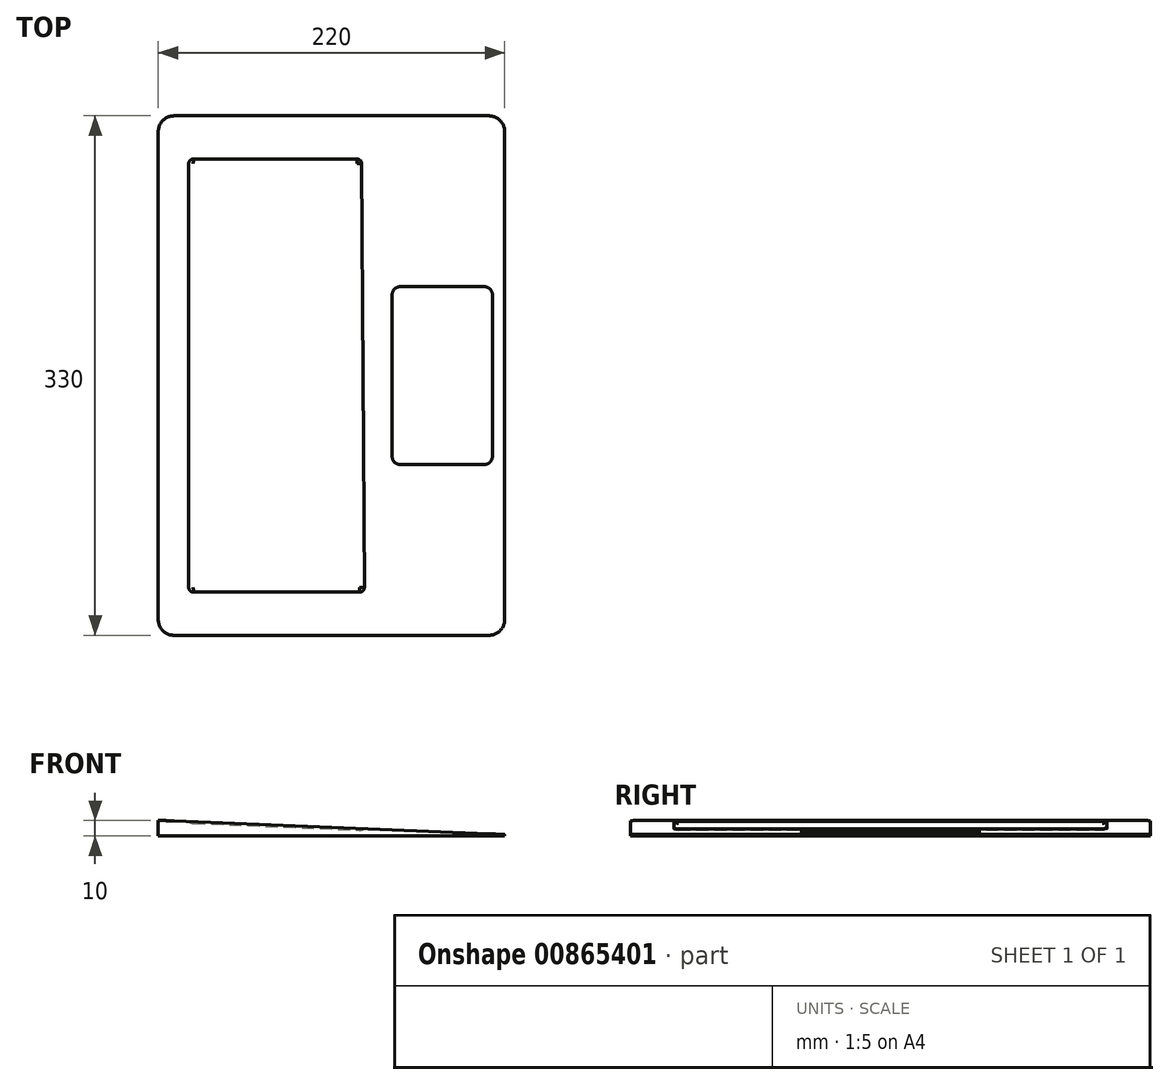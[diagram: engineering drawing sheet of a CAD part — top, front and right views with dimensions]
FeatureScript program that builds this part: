
annotation { "Feature Type Name" : "Feature", "Feature Type Description" : "" }
export const myFeature = defineFeature(function(context is Context, id is Id, definition is map)
    precondition{}
    {
        {
            var Q0;
            Q0=qCreatedBy(makeId("Front.planeOp"),FACE);
            var sketch = newSketch(context, id + "F0", { "sketchPlane" : qUnion([Q0])});
            skLineSegment(sketch, "E0", {"start": v(-46.92, 6.77) * mm, "end": v(-46.92, -3.23) * mm});
            skLineSegment(sketch, "E1", {"start": v(-46.92, -3.23) * mm, "end": v(173.08, -3.23) * mm});
            skLineSegment(sketch, "E2", {"start": v(173.08, -3.23) * mm, "end": v(173.08, -2.23) * mm});
            skLineSegment(sketch, "E3", {"start": v(173.08, -2.23) * mm, "end": v(-46.92, 6.77) * mm});
            skSolve(sketch);
        }
        {
            var Q0;
            Q0=makeQuery(id+"F0.imprint","IMPRINT",FACE,{"disambiguationData":[TD([[makeQuery(id+"F0.imprint","IMPRINT",EDGE,{"derivedFrom":sQuery(id+"F0.wireOp",EDGE,"E0")}),1.0]])]});
            extrude(context, id + "F1", {"entities" : qUnion([Q0]), "oppositeDirection" : true, "depth" : 330 * mm, "offsetDistance" : 25 * mm});
        }
        {
            var Q0;
            Q0=makeQuery(id+"F1.opExtrude","CAP_EDGE",EDGE,{"disambiguationData":[OSD([sQuery(id+"F0.wireOp",EDGE,"E0")])],"isStart":true});
            fillet(context, id + "F2", {"entities" : qUnion([Q0]), "radius" : 10 * mm, "tangentPropagation" : true, "allowEdgeOverflow" : false});
        }
        {
            var Q0;
            Q0=makeQuery(id+"F1.opExtrude","CAP_EDGE",EDGE,{"disambiguationData":[OSD([sQuery(id+"F0.wireOp",EDGE,"E0")])],"isStart":false});
            fillet(context, id + "F3", {"entities" : qUnion([Q0]), "radius" : 10 * mm, "tangentPropagation" : true, "allowEdgeOverflow" : false});
        }
        {
            var Q0;
            Q0=makeQuery(id+"F1.opExtrude","SWEPT_FACE",FACE,{"disambiguationData":[OSD([sQuery(id+"F0.wireOp",EDGE,"E3")])]});
            var sketch = newSketch(context, id + "F4", { "sketchPlane" : qUnion([Q0])});
            skLineSegment(sketch, "E4", {"start": v(0, 0) * mm, "end": v(-46.11, 10) * mm});
            skLineSegment(sketch, "E5", {"start": v(-46.11, 10) * mm, "end": v(-46.11, 0) * mm});
            skLineSegment(sketch, "E6", {"start": v(-46.11, 0) * mm, "end": v(-46.11, 330) * mm});
            skLineSegment(sketch, "E7", {"start": v(-46.11, 330) * mm, "end": v(173.89, 330) * mm});
            skLineSegment(sketch, "E8", {"start": v(173.89, 330) * mm, "end": v(173.89, 0) * mm});
            skLineSegment(sketch, "E9", {"start": v(173.89, 0) * mm, "end": v(-46.11, 0) * mm});
            skLineSegment(sketch, "E10", {"start": v(173.89, 330) * mm, "end": v(-46.11, 0) * mm});
            skLineSegment(sketch, "E11", {"start": v(-46.11, 0) * mm, "end": v(-27.8, 27.46) * mm});
            skLineSegment(sketch, "E12", {"start": v(173.89, 330) * mm, "end": v(155.58, 302.54) * mm});
            skLineSegment(sketch, "E13", {"start": v(-46.11, 330) * mm, "end": v(173.89, 0) * mm});
            skLineSegment(sketch, "E14", {"start": v(-46.11, 330) * mm, "end": v(-27.8, 302.54) * mm});
            skLineSegment(sketch, "E15", {"start": v(173.89, 0) * mm, "end": v(155.58, 27.46) * mm});
            skLineSegment(sketch, "E16", {"start": v(-27.8, 302.54) * mm, "end": v(-27.8, 27.46) * mm});
            skLineSegment(sketch, "E17", {"start": v(-27.8, 27.46) * mm, "end": v(83.9, 27.46) * mm});
            skLineSegment(sketch, "E18", {"start": v(-27.8, 302.54) * mm, "end": v(82.2, 302.54) * mm});
            skLineSegment(sketch, "E19", {"start": v(82.2, 302.54) * mm, "end": v(83.9, 27.46) * mm});
            skLineSegment(sketch, "E20", {"start": v(83.23, 135.99) * mm, "end": v(101.53, 108.53) * mm});
            skLineSegment(sketch, "E21", {"start": v(101.53, 108.53) * mm, "end": v(101.53, 221.47) * mm});
            skLineSegment(sketch, "E22", {"start": v(101.53, 221.47) * mm, "end": v(165.25, 221.47) * mm});
            skLineSegment(sketch, "E23", {"start": v(165.25, 221.47) * mm, "end": v(165.25, 108.53) * mm});
            skLineSegment(sketch, "E24", {"start": v(165.25, 108.53) * mm, "end": v(101.53, 108.53) * mm});
            skSolve(sketch);
        }
        {
            var Q0;
            {var subQ5=sQuery(id+"F4.wireOp",EDGE,"E18");Q0=makeQuery(id+"F4.imprint","IMPRINT",FACE,{"disambiguationData":[TD([[makeQuery(id+"F4.imprint","IMPRINT",EDGE,{"derivedFrom":subQ5}),-1.0]])]});}
            var Q1;
            {var subQ0=sQuery(id+"F4.wireOp",EDGE,"E16");Q1=makeQuery(id+"F4.imprint","IMPRINT",FACE,{"disambiguationData":[TD([[makeQuery(id+"F4.imprint","IMPRINT",EDGE,{"derivedFrom":subQ0}),1.0]])]});}
            var Q2;
            {var subQ0=sQuery(id+"F4.wireOp",EDGE,"E19");var subQ1=sQuery(id+"F4.wireOp",EDGE,"E10");var subQ2=makeQuery(id+"F4.imprint","INTERSECT",VERTEX,{"derivedFrom":[subQ1,subQ0]});Q2=makeQuery(id+"F4.imprint","IMPRINT",FACE,{"disambiguationData":[TD([[makeQuery(id+"F4.imprint","IMPRINT",EDGE,{"disambiguationData":[TD([[subQ2,-1.0]])],"derivedFrom":subQ1}),1.0]])]});}
            var Q3;
            {var subQ0=sQuery(id+"F4.wireOp",EDGE,"E17");Q3=makeQuery(id+"F4.imprint","IMPRINT",FACE,{"disambiguationData":[TD([[makeQuery(id+"F4.imprint","IMPRINT",EDGE,{"derivedFrom":subQ0}),1.0]])]});}
            extrude(context, id + "F5", {"entities" : qUnion([Q0, Q1, Q2, Q3]), "operationType" : NewBodyOperationType.REMOVE, "oppositeDirection" : true, "depth" : 1 * mm, "offsetDistance" : 25 * mm});
        }
        {
            var Q0;
            Q0=makeQuery(id+"F5.boolean.opBoolean","COPY",EDGE,{"derivedFrom":makeQuery(id+"F5.opExtrude","CAP_EDGE",EDGE,{"disambiguationData":[OSD([sQuery(id+"F4.wireOp",EDGE,"E16")])],"isStart":false})});
            var Q1;
            Q1=makeQuery(id+"F5.boolean.opBoolean","COPY",EDGE,{"derivedFrom":makeQuery(id+"F5.opExtrude","CAP_EDGE",EDGE,{"disambiguationData":[OSD([sQuery(id+"F4.wireOp",EDGE,"E17")])],"isStart":false})});
            var Q2;
            Q2=makeQuery(id+"F5.boolean.opBoolean","COPY",EDGE,{"derivedFrom":makeQuery(id+"F5.opExtrude","CAP_EDGE",EDGE,{"disambiguationData":[OSD([sQuery(id+"F4.wireOp",EDGE,"E19")])],"isStart":false})});
            var Q3;
            Q3=makeQuery(id+"F5.boolean.opBoolean","COPY",EDGE,{"derivedFrom":makeQuery(id+"F5.opExtrude","CAP_EDGE",EDGE,{"disambiguationData":[OSD([sQuery(id+"F4.wireOp",EDGE,"E18")])],"isStart":false})});
            fillet(context, id + "F6", {"entities" : qUnion([Q0, Q1, Q2, Q3]), "radius" : 5 * mm, "tangentPropagation" : true, "allowEdgeOverflow" : false});
        }
        {
            var Q0;
            Q0=makeQuery(id+"F4.imprint","IMPRINT",FACE,{"disambiguationData":[TD([[makeQuery(id+"F4.imprint","IMPRINT",EDGE,{"derivedFrom":sQuery(id+"F4.wireOp",EDGE,"E21")}),-1.0]])]});
            extrude(context, id + "F7", {"entities" : qUnion([Q0]), "operationType" : NewBodyOperationType.REMOVE, "oppositeDirection" : true, "depth" : 0.5 * mm, "offsetDistance" : 25 * mm});
        }
        {
            var Q0;
            Q0=makeQuery(id+"F6.opFillet","BLEND_EDGE",EDGE,{"blendedFrom":[makeQuery(id+"F5.boolean.opBoolean","COPY",EDGE,{"derivedFrom":makeQuery(id+"F5.opExtrude","CAP_EDGE",EDGE,{"disambiguationData":[OSD([sQuery(id+"F4.wireOp",EDGE,"E17")])],"isStart":false})}),makeQuery(id+"F5.boolean.opBoolean","COPY",EDGE,{"derivedFrom":makeQuery(id+"F5.opExtrude","CAP_EDGE",EDGE,{"disambiguationData":[OSD([sQuery(id+"F4.wireOp",EDGE,"E19")])],"isStart":false})})],"blendedInto":[]});
            fillet(context, id + "F8", {"entities" : qUnion([Q0]), "radius" : 5 * mm, "tangentPropagation" : true, "allowEdgeOverflow" : false});
        }
        {
            var Q0;
            Q0=makeQuery(id+"F6.opFillet","BLEND_EDGE",EDGE,{"blendedFrom":[makeQuery(id+"F5.boolean.opBoolean","COPY",EDGE,{"derivedFrom":makeQuery(id+"F5.opExtrude","CAP_EDGE",EDGE,{"disambiguationData":[OSD([sQuery(id+"F4.wireOp",EDGE,"E18")])],"isStart":false})}),makeQuery(id+"F5.boolean.opBoolean","COPY",EDGE,{"derivedFrom":makeQuery(id+"F5.opExtrude","CAP_EDGE",EDGE,{"disambiguationData":[OSD([sQuery(id+"F4.wireOp",EDGE,"E19")])],"isStart":false})})],"blendedInto":[]});
            var Q1;
            Q1=makeQuery(id+"F6.opFillet","BLEND_EDGE",EDGE,{"blendedFrom":[makeQuery(id+"F5.boolean.opBoolean","COPY",EDGE,{"derivedFrom":makeQuery(id+"F5.opExtrude","CAP_EDGE",EDGE,{"disambiguationData":[OSD([sQuery(id+"F4.wireOp",EDGE,"E16")])],"isStart":false})}),makeQuery(id+"F5.boolean.opBoolean","COPY",EDGE,{"derivedFrom":makeQuery(id+"F5.opExtrude","CAP_EDGE",EDGE,{"disambiguationData":[OSD([sQuery(id+"F4.wireOp",EDGE,"E18")])],"isStart":false})})],"blendedInto":[]});
            var Q2;
            Q2=makeQuery(id+"F6.opFillet","BLEND_EDGE",EDGE,{"blendedFrom":[makeQuery(id+"F5.boolean.opBoolean","COPY",EDGE,{"derivedFrom":makeQuery(id+"F5.opExtrude","CAP_EDGE",EDGE,{"disambiguationData":[OSD([sQuery(id+"F4.wireOp",EDGE,"E16")])],"isStart":false})}),makeQuery(id+"F5.boolean.opBoolean","COPY",EDGE,{"derivedFrom":makeQuery(id+"F5.opExtrude","CAP_EDGE",EDGE,{"disambiguationData":[OSD([sQuery(id+"F4.wireOp",EDGE,"E17")])],"isStart":false})})],"blendedInto":[]});
            var Q3;
            Q3=makeQuery(id+"F7.boolean.opBoolean","COPY",EDGE,{"derivedFrom":makeQuery(id+"F7.opExtrude","SWEPT_EDGE",EDGE,{"disambiguationData":[OSD([sQuery(id+"F4.wireOp",EDGE,"E10"),sQuery(id+"F4.wireOp",EDGE,"E21"),sQuery(id+"F4.wireOp",EDGE,"E22")])]})});
            var Q4;
            Q4=makeQuery(id+"F7.boolean.opBoolean","COPY",EDGE,{"derivedFrom":makeQuery(id+"F7.opExtrude","SWEPT_EDGE",EDGE,{"disambiguationData":[OSD([sQuery(id+"F4.wireOp",EDGE,"E22"),sQuery(id+"F4.wireOp",EDGE,"E23")])]})});
            var Q5;
            Q5=makeQuery(id+"F7.boolean.opBoolean","COPY",EDGE,{"derivedFrom":makeQuery(id+"F7.opExtrude","SWEPT_EDGE",EDGE,{"disambiguationData":[OSD([sQuery(id+"F4.wireOp",EDGE,"E13"),sQuery(id+"F4.wireOp",EDGE,"E20"),sQuery(id+"F4.wireOp",EDGE,"E21"),sQuery(id+"F4.wireOp",EDGE,"E24")])]})});
            var Q6;
            Q6=makeQuery(id+"F7.boolean.opBoolean","COPY",EDGE,{"derivedFrom":makeQuery(id+"F7.opExtrude","SWEPT_EDGE",EDGE,{"disambiguationData":[OSD([sQuery(id+"F4.wireOp",EDGE,"E23"),sQuery(id+"F4.wireOp",EDGE,"E24")])]})});
            fillet(context, id + "F9", {"entities" : qUnion([Q0, Q1, Q2, Q3, Q4, Q5, Q6]), "radius" : 5 * mm, "tangentPropagation" : true, "allowEdgeOverflow" : false});
        }
        {
            var Q0;
            Q0=makeQuery(id+"F1.opExtrude","CAP_EDGE",EDGE,{"disambiguationData":[OSD([sQuery(id+"F0.wireOp",EDGE,"E2")])],"isStart":true});
            var Q1;
            Q1=makeQuery(id+"F1.opExtrude","CAP_EDGE",EDGE,{"disambiguationData":[OSD([sQuery(id+"F0.wireOp",EDGE,"E2")])],"isStart":false});
            fillet(context, id + "F10", {"entities" : qUnion([Q0, Q1]), "radius" : 10 * mm, "tangentPropagation" : true, "allowEdgeOverflow" : false});
        }
    });
